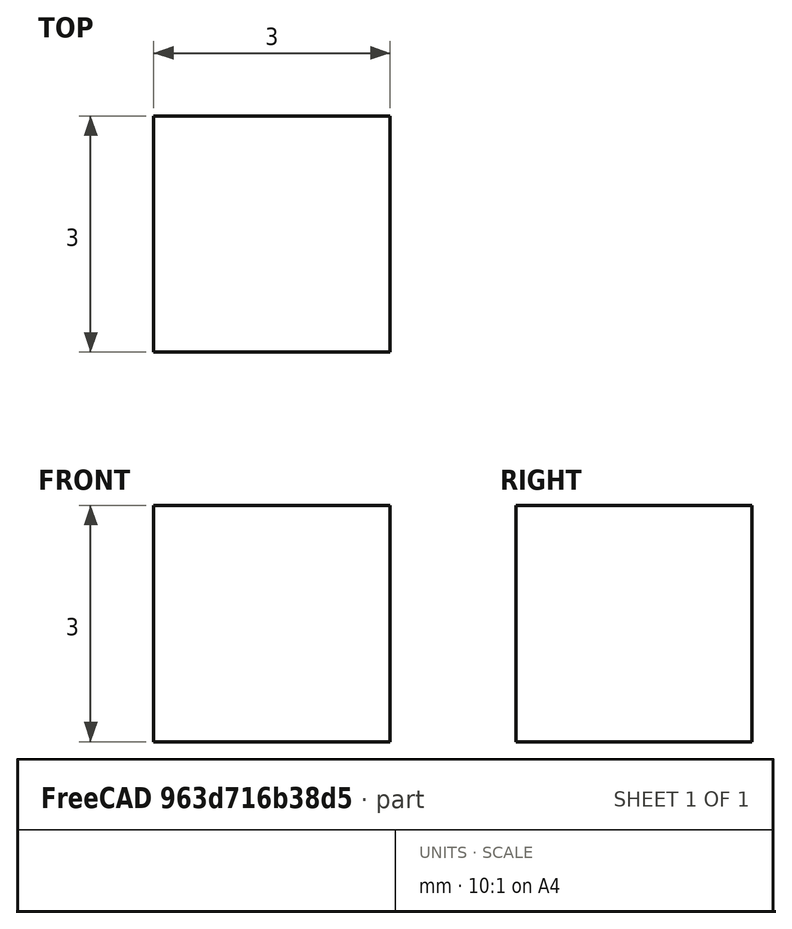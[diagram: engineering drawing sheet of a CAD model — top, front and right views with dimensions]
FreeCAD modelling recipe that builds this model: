
FCSTD DOCUMENT  (FreeCAD 0.19R24276 (Git))
Label: L3mm
License: All rights reserved
LicenseURL: http://en.wikipedia.org/wiki/All_rights_reserved
objects: Sketcher::SketchObject×1, PartDesign::Pad×1, PartDesign::Body×1
note: 4 computed .brp shape members not serialized (recipe doc carries the construction recipe); baked Part::Feature solids carry a one-line shape summary decoded from their .brp

FEATURE [Sketcher::SketchObject] Sketch
  FullyConstrained = true
  MapMode = 5
  Support = -> [XY_Plane]
  sketch-geometry (4):
    g0: LineSegment StartX=0 StartY=0 StartZ=0 EndX=3 EndY=0 EndZ=0
    g1: LineSegment StartX=3 StartY=0 StartZ=0 EndX=3 EndY=3 EndZ=0
    g2: LineSegment StartX=3 StartY=3 StartZ=0 EndX=0 EndY=3 EndZ=0
    g3: LineSegment StartX=0 StartY=3 StartZ=0 EndX=0 EndY=0 EndZ=0
  constraints (11):
    c: Coincident(g0,g1)
    c: Coincident(g1,g2)
    c: Coincident(g2,g3)
    c: Coincident(g3,g0)
    c: Horizontal(g0)
    c: Horizontal(g2)
    c: Vertical(g1)
    c: Vertical(g3)
    c: Coincident(g0,g-1)
    c: DistanceY(g1,g1) = 3
    c: DistanceX(g0,g0) = 3
FEATURE [PartDesign::Pad] Pad
  Direction = (1,1,1)
  Length = 3
  Length2 = 100
  Profile = -> Sketch
  Type = 0
FEATURE [PartDesign::Body] Body
  Group = -> [Sketch,Pad]
  Origin = -> Origin
  Tip = -> Pad
